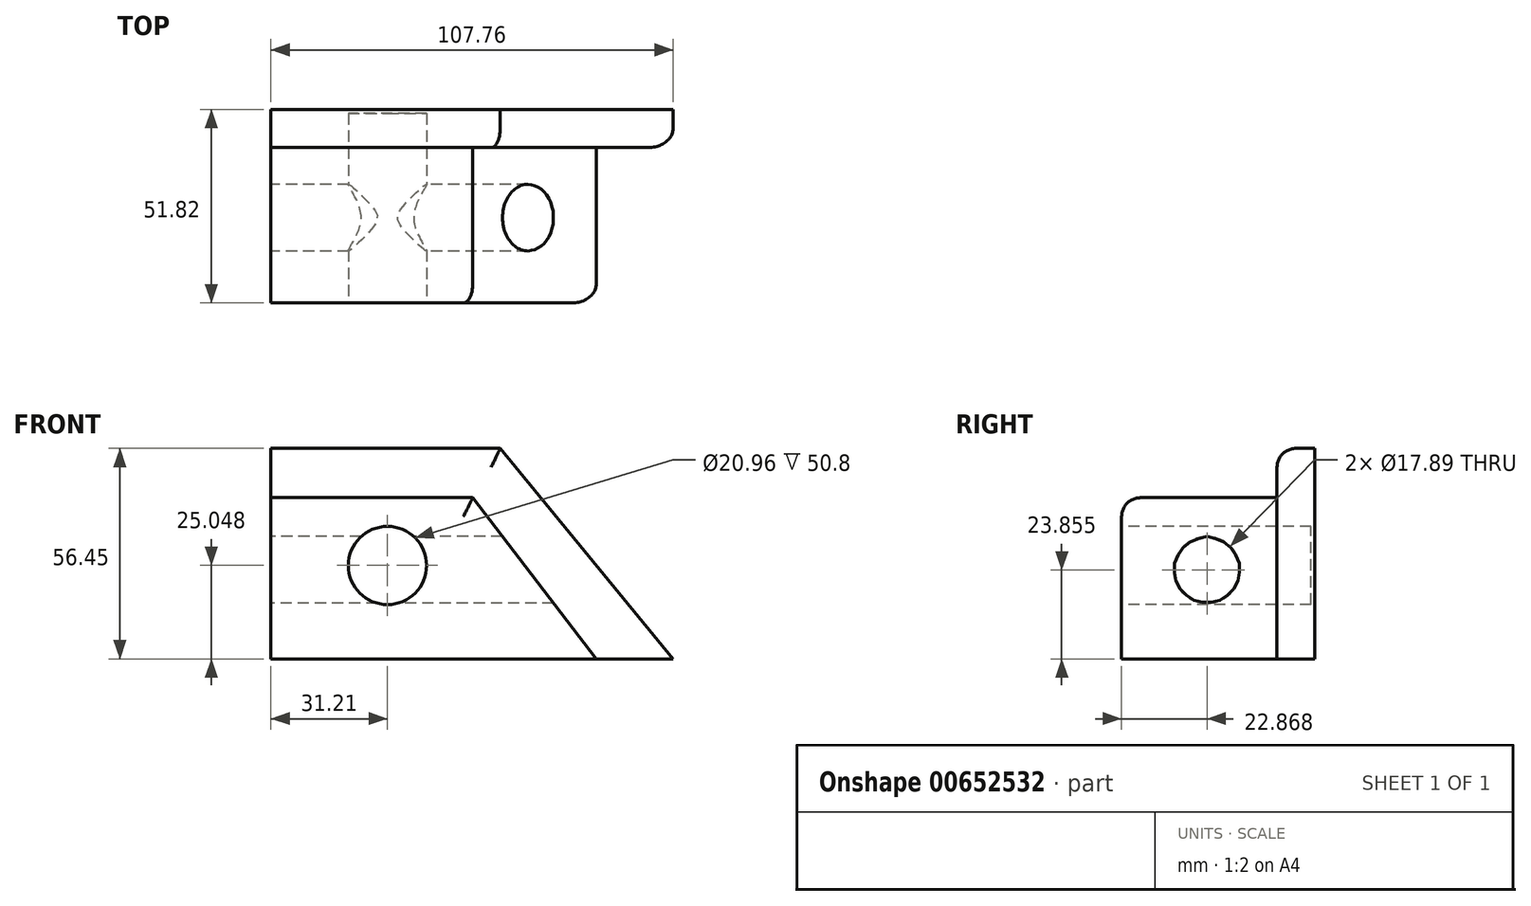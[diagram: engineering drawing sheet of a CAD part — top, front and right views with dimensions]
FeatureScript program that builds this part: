
annotation { "Feature Type Name" : "Feature", "Feature Type Description" : "" }
export const myFeature = defineFeature(function(context is Context, id is Id, definition is map)
    precondition{}
    {
        {
            var Q0;
            Q0=qCreatedBy(makeId("Front.planeOp"),FACE);
            var sketch = newSketch(context, id + "F0", { "sketchPlane" : qUnion([Q0])});
            skLineSegment(sketch, "E0", {"start": v(0, 56.45) * mm, "end": v(61.42, 56.45) * mm});
            skLineSegment(sketch, "E1", {"start": v(61.42, 56.45) * mm, "end": v(107.76, 0) * mm});
            skLineSegment(sketch, "E2", {"start": v(107.76, 0) * mm, "end": v(0, 0) * mm});
            skLineSegment(sketch, "E3", {"start": v(0, 56.45) * mm, "end": v(0, 0) * mm});
            skLineSegment(sketch, "E4", {"start": v(0, 43.21) * mm, "end": v(54.06, 43.21) * mm});
            skLineSegment(sketch, "E5", {"start": v(54.06, 43.21) * mm, "end": v(87.16, 0) * mm});
            skSolve(sketch);
        }
        {
            var Q0;
            {var subQ4=sQuery(id+"F0.wireOp",EDGE,"E4");Q0=makeQuery(id+"F0.imprint","IMPRINT",FACE,{"disambiguationData":[TD([[makeQuery(id+"F0.imprint","IMPRINT",EDGE,{"derivedFrom":subQ4}),-1.0]])]});}
            extrude(context, id + "F1", {"entities" : qUnion([Q0]), "depth" : 51.82 * mm, "offsetDistance" : 25.4 * mm});
        }
        {
            var Q0;
            {var subQ1=sQuery(id+"F0.wireOp",EDGE,"E0");Q0=makeQuery(id+"F0.imprint","IMPRINT",FACE,{"disambiguationData":[TD([[makeQuery(id+"F0.imprint","IMPRINT",EDGE,{"derivedFrom":subQ1}),-1.0]])]});}
            extrude(context, id + "F2", {"entities" : qUnion([Q0]), "operationType" : NewBodyOperationType.ADD, "depth" : 10.16 * mm, "offsetDistance" : 25.4 * mm});
        }
        {
            var Q0;
            Q0=qCreatedBy(makeId("Right.planeOp"),FACE);
            var sketch = newSketch(context, id + "F3", { "sketchPlane" : qUnion([Q0])});
            skCircle(sketch, "E6", {"center": v(-28.95, 23.85) * mm, "radius": 8.94 * mm});
            skSolve(sketch);
        }
        {
            var Q0;
            Q0 = qSketchRegion(id + "F3", true);
            extrude(context, id + "F4", {"entities" : qUnion([Q0]), "operationType" : NewBodyOperationType.REMOVE, "depth" : 101.6 * mm, "offsetDistance" : 25.4 * mm});
        }
        {
            var Q0;
            Q0=makeQuery(id+"F1.opExtrude","CAP_FACE",FACE,{"disambiguationData":[OSD([sQuery(id+"F0.wireOp",EDGE,"E2"),sQuery(id+"F0.wireOp",EDGE,"E3"),sQuery(id+"F0.wireOp",EDGE,"E4"),sQuery(id+"F0.wireOp",EDGE,"E5")])],"isStart":false});
            var sketch = newSketch(context, id + "F5", { "sketchPlane" : qUnion([Q0])});
            skCircle(sketch, "E7", {"center": v(32.87, 25.29) * mm, "radius": 9.22 * mm});
            skSolve(sketch);
        }
        {
            var Q0;
            Q0=makeQuery(id+"F5.imprint","IMPRINT",FACE,{"disambiguationData":[TD([[makeQuery(id+"F5.imprint","IMPRINT",EDGE,{"derivedFrom":sQuery(id+"F5.wireOp",EDGE,"E7")}),1.0]])]});
            extrude(context, id + "F6", {"entities" : qUnion([Q0]), "operationType" : NewBodyOperationType.REMOVE, "depth" : 50.8 * mm, "offsetDistance" : 25.4 * mm});
        }
        {
            var Q0;
            Q0=makeQuery(id+"F1.opExtrude","CAP_FACE",FACE,{"disambiguationData":[OSD([sQuery(id+"F0.wireOp",EDGE,"E2"),sQuery(id+"F0.wireOp",EDGE,"E3"),sQuery(id+"F0.wireOp",EDGE,"E4"),sQuery(id+"F0.wireOp",EDGE,"E5")])],"isStart":false});
            var sketch = newSketch(context, id + "F7", { "sketchPlane" : qUnion([Q0])});
            skCircle(sketch, "E8", {"center": v(31.21, 25.05) * mm, "radius": 10.48 * mm});
            skSolve(sketch);
        }
        {
            var Q0;
            Q0 = qSketchRegion(id + "F7", true);
            extrude(context, id + "F8", {"entities" : qUnion([Q0]), "operationType" : NewBodyOperationType.REMOVE, "oppositeDirection" : true, "depth" : 50.8 * mm, "offsetDistance" : 25.4 * mm});
        }
        {
            var Q0;
            Q0=makeQuery(id+"F2.opExtrude","CAP_EDGE",EDGE,{"disambiguationData":[OSD([sQuery(id+"F0.wireOp",EDGE,"E0")])],"isStart":false});
            var Q1;
            Q1=makeQuery(id+"F2.opExtrude","CAP_EDGE",EDGE,{"disambiguationData":[OSD([sQuery(id+"F0.wireOp",EDGE,"E1")])],"isStart":false});
            var Q2;
            Q2=makeQuery(id+"F1.opExtrude","CAP_EDGE",EDGE,{"disambiguationData":[OSD([sQuery(id+"F0.wireOp",EDGE,"E4")])],"isStart":false});
            var Q3;
            Q3=makeQuery(id+"F1.opExtrude","CAP_EDGE",EDGE,{"disambiguationData":[OSD([sQuery(id+"F0.wireOp",EDGE,"E5")])],"isStart":false});
            fillet(context, id + "F9", {"entities" : qUnion([Q0, Q1, Q2, Q3]), "radius" : 5.08 * mm, "tangentPropagation" : true, "allowEdgeOverflow" : false});
        }
    });
